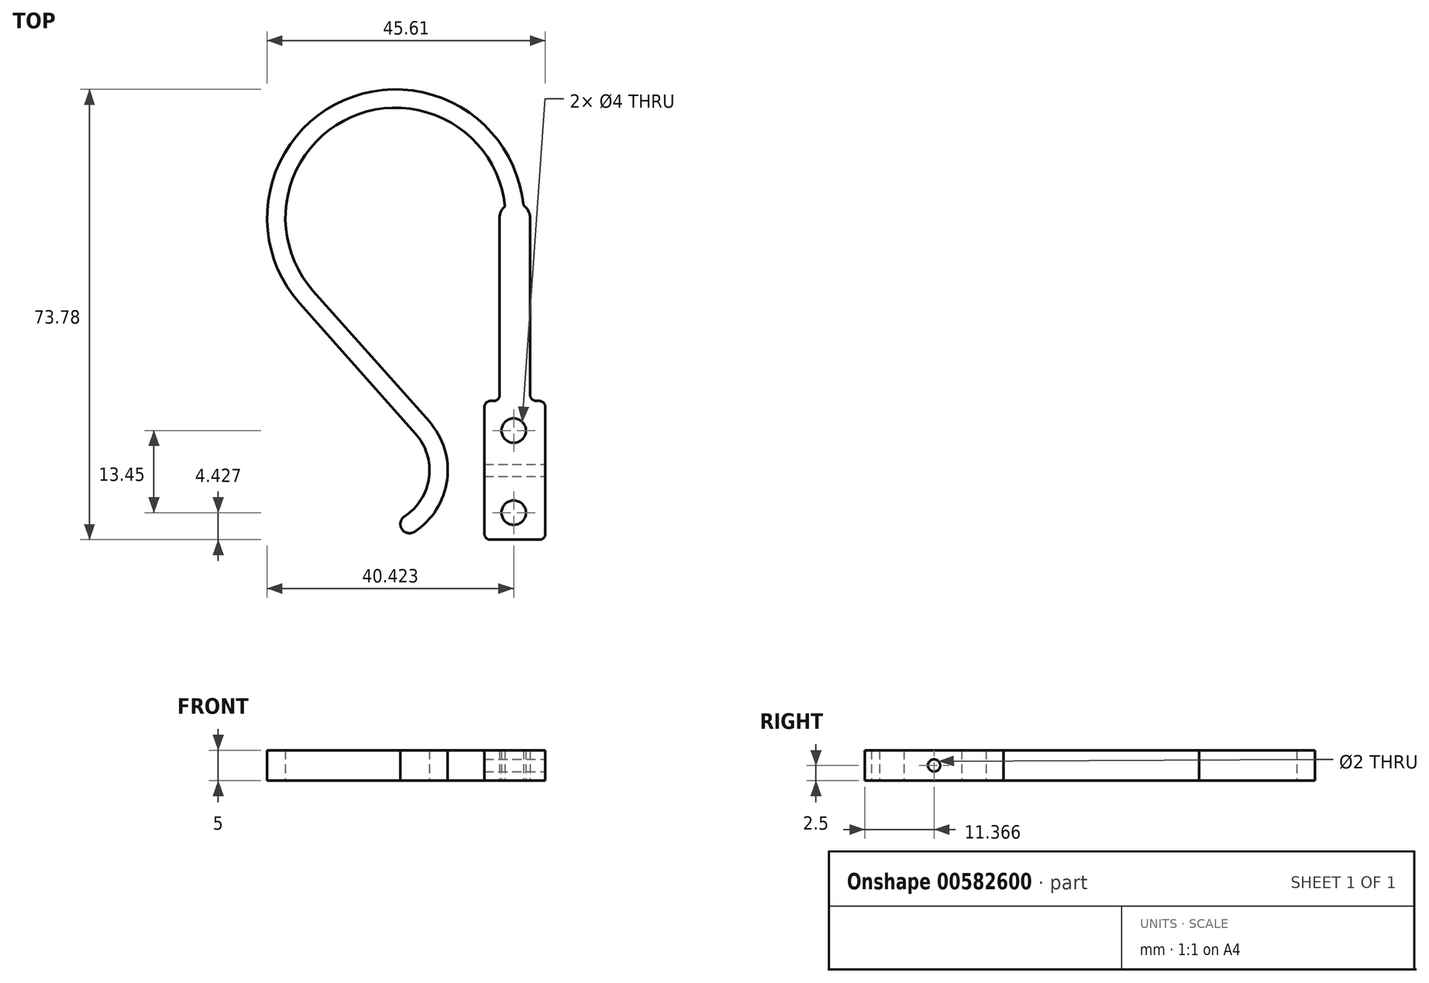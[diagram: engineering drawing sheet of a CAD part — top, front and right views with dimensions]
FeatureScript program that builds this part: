
annotation { "Feature Type Name" : "Feature", "Feature Type Description" : "" }
export const myFeature = defineFeature(function(context is Context, id is Id, definition is map)
    precondition{}
    {
        {
            var Q0;
            Q0=qCreatedBy(makeId("Top.planeOp"),FACE);
            var sketch = newSketch(context, id + "F0", { "sketchPlane" : qUnion([Q0])});
            skLineSegment(sketch, "E0.bottom", {"start": v(0, 0) * mm, "end": v(10, 0) * mm});
            skLineSegment(sketch, "E0.top", {"start": v(0, 22.73) * mm, "end": v(10, 22.73) * mm});
            skLineSegment(sketch, "E0.left", {"start": v(0, 0) * mm, "end": v(0, 22.73) * mm});
            skLineSegment(sketch, "E0.right", {"start": v(10, 0) * mm, "end": v(10, 22.73) * mm});
            skLineSegment(sketch, "E1", {"start": v(5, 22.73) * mm, "end": v(5, 52.73) * mm});
            skArc(sketch, "E2", {"start": v(5, 52.73) * mm, "mid": v(-21.5, 71) * mm, "end": v(-29.17, 39.74) * mm});
            skLineSegment(sketch, "E3", {"start": v(-29.17, 39.74) * mm, "end": v(-10.16, 18.36) * mm});
            skArc(sketch, "E4", {"start": v(-10.16, 18.36) * mm, "mid": v(-7.6, 9.98) * mm, "end": v(-12.26, 2.56) * mm});
            skArc(sketch, "E5.0.endCap", {"start": v(2.5, 52.73) * mm, "mid": v(5, 55.23) * mm, "end": v(7.5, 52.73) * mm});
            skLineSegment(sketch, "E5.0.left", {"start": v(2.5, 22.73) * mm, "end": v(2.5, 52.73) * mm});
            skLineSegment(sketch, "E5.0.right", {"start": v(7.5, 22.73) * mm, "end": v(7.5, 52.73) * mm});
            skArc(sketch, "E6.0.startCap", {"start": v(6.5, 52.73) * mm, "mid": v(5, 51.23) * mm, "end": v(3.5, 52.73) * mm});
            skArc(sketch, "E6.0.endCap", {"start": v(-28.04, 40.74) * mm, "mid": v(-28.17, 38.62) * mm, "end": v(-30.29, 38.74) * mm});
            skArc(sketch, "E6.0.left", {"start": v(3.5, 52.73) * mm, "mid": v(-20.97, 69.6) * mm, "end": v(-28.04, 40.74) * mm});
            skArc(sketch, "E6.0.right", {"start": v(6.5, 52.73) * mm, "mid": v(-22.04, 72.41) * mm, "end": v(-30.29, 38.74) * mm});
            skArc(sketch, "E6.1.startCap", {"start": v(-30.29, 38.74) * mm, "mid": v(-30.16, 40.86) * mm, "end": v(-28.04, 40.74) * mm});
            skArc(sketch, "E6.1.endCap", {"start": v(-9.04, 19.36) * mm, "mid": v(-9.16, 17.24) * mm, "end": v(-11.28, 17.37) * mm});
            skLineSegment(sketch, "E6.1.left", {"start": v(-28.04, 40.74) * mm, "end": v(-9.04, 19.36) * mm});
            skLineSegment(sketch, "E6.1.right", {"start": v(-30.29, 38.74) * mm, "end": v(-11.28, 17.37) * mm});
            skArc(sketch, "E6.2.startCap", {"start": v(-11.28, 17.37) * mm, "mid": v(-11.16, 19.48) * mm, "end": v(-9.04, 19.36) * mm});
            skArc(sketch, "E6.2.endCap", {"start": v(-11.44, 1.3) * mm, "mid": v(-13.51, 1.74) * mm, "end": v(-13.08, 3.81) * mm});
            skArc(sketch, "E6.2.left", {"start": v(-9.04, 19.36) * mm, "mid": v(-6.1, 9.78) * mm, "end": v(-11.44, 1.3) * mm});
            skArc(sketch, "E6.2.right", {"start": v(-11.28, 17.37) * mm, "mid": v(-9.08, 10.18) * mm, "end": v(-13.08, 3.81) * mm});
            skPoint(sketch, "E7", {"position": v(0, 11.37) * mm});
            skCircle(sketch, "E8", {"center": v(4.81, 17.88) * mm, "radius": 2 * mm});
            skCircle(sketch, "E9", {"center": v(4.81, 4.43) * mm, "radius": 2 * mm});
            skSolve(sketch);
        }
        {
            var Q0;
            Q0 = qSketchRegion(id + "F0", true);
            extrude(context, id + "F1", {"entities" : qUnion([Q0]), "depth" : 5 * mm, "offsetDistance" : 25 * mm});
        }
        {
            var Q0;
            Q0=makeQuery(id+"F1.opExtrude","SWEPT_EDGE",EDGE,{"disambiguationData":[OSD([sQuery(id+"F0.wireOp",EDGE,"E0.top"),sQuery(id+"F0.wireOp",EDGE,"E0.left")])]});
            var Q1;
            Q1=makeQuery(id+"F1.opExtrude","SWEPT_EDGE",EDGE,{"disambiguationData":[OSD([sQuery(id+"F0.wireOp",EDGE,"E0.top"),sQuery(id+"F0.wireOp",EDGE,"E5.0.left")])]});
            var Q2;
            Q2=makeQuery(id+"F1.opExtrude","SWEPT_EDGE",EDGE,{"disambiguationData":[OSD([sQuery(id+"F0.wireOp",EDGE,"E0.top"),sQuery(id+"F0.wireOp",EDGE,"E0.right")])]});
            var Q3;
            Q3=makeQuery(id+"F1.opExtrude","SWEPT_EDGE",EDGE,{"disambiguationData":[OSD([sQuery(id+"F0.wireOp",EDGE,"E0.top"),sQuery(id+"F0.wireOp",EDGE,"E5.0.right")])]});
            var Q4;
            Q4=makeQuery(id+"F1.opExtrude","SWEPT_EDGE",EDGE,{"disambiguationData":[OSD([sQuery(id+"F0.wireOp",EDGE,"E0.bottom"),sQuery(id+"F0.wireOp",EDGE,"E0.right")])]});
            var Q5;
            Q5=makeQuery(id+"F1.opExtrude","SWEPT_EDGE",EDGE,{"disambiguationData":[OSD([sQuery(id+"F0.wireOp",EDGE,"E0.bottom"),sQuery(id+"F0.wireOp",EDGE,"E0.left")])]});
            fillet(context, id + "F2", {"entities" : qUnion([Q0, Q1, Q2, Q3, Q4, Q5]), "radius" : 1 * mm, "tangentPropagation" : true, "allowEdgeOverflow" : false});
        }
        {
            var Q0;
            Q0=makeQuery(id+"F1.opExtrude","SWEPT_FACE",FACE,{"disambiguationData":[OSD([sQuery(id+"F0.wireOp",EDGE,"E0.right")])]});
            var sketch = newSketch(context, id + "F3", { "sketchPlane" : qUnion([Q0])});
            skCircle(sketch, "E10", {"center": v(11.37, 2.5) * mm, "radius": 1 * mm});
            skPoint(sketch, "E10.centerSnap0", {"position": v(11.37, 5) * mm});
            skPoint(sketch, "E11", {"position": v(11.37, 0) * mm});
            skSolve(sketch);
        }
        {
            var Q0;
            Q0 = qSketchRegion(id + "F3", true);
            extrude(context, id + "F4", {"entities" : qUnion([Q0]), "operationType" : NewBodyOperationType.REMOVE, "endBound" : BoundingType.UP_TO_NEXT, "oppositeDirection" : true, "depth" : 25 * mm, "offsetDistance" : 25 * mm});
        }
    });
